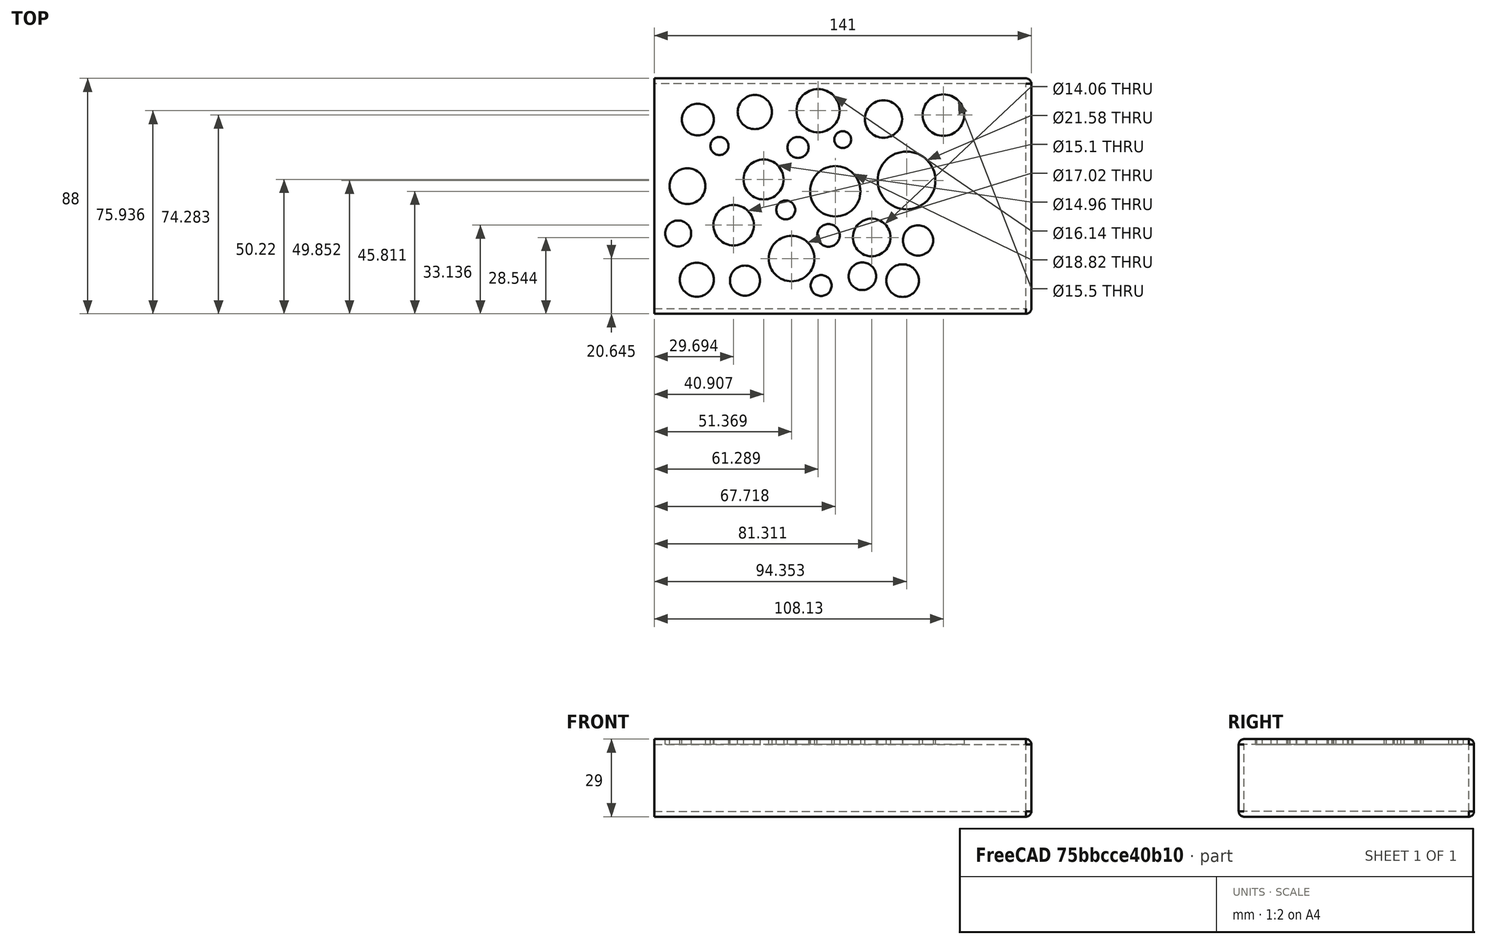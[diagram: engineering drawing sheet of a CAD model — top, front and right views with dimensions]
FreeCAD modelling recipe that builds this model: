
FCSTD DOCUMENT  (FreeCAD 0.18R4 (GitTag))
Label: V4
License: All rights reserved
LicenseURL: http://en.wikipedia.org/wiki/All_rights_reserved
objects: Sketcher::SketchObject×2, PartDesign::Pad×1, PartDesign::Thickness×1, PartDesign::Pocket×1, PartDesign::Body×1
note: 8 computed .brp shape members not serialized (recipe doc carries the construction recipe); baked Part::Feature solids carry a one-line shape summary decoded from their .brp

FEATURE [Sketcher::SketchObject] Sketch001
  MapMode = 5
  sketch-geometry (4):
    g0: LineSegment StartX=-98.6361 StartY=-55.4136 StartZ=0 EndX=40.3639 EndY=-55.4136 EndZ=0
    g1: LineSegment StartX=40.3639 StartY=-55.4136 StartZ=0 EndX=40.3639 EndY=28.5864 EndZ=0
    g2: LineSegment StartX=40.3639 StartY=28.5864 StartZ=0 EndX=-98.6361 EndY=28.5864 EndZ=0
    g3: LineSegment StartX=-98.6361 StartY=28.5864 StartZ=0 EndX=-98.6361 EndY=-55.4136 EndZ=0
  constraints (10):
    c: Coincident(g0,g1)
    c: Coincident(g1,g2)
    c: Coincident(g2,g3)
    c: Coincident(g3,g0)
    c: Horizontal(g0)
    c: Horizontal(g2)
    c: Vertical(g1)
    c: Vertical(g3)
    c: DistanceY(g0,g1) = 84
    c: DistanceX(g2,g1) = 139
FEATURE [PartDesign::Pad] Pad
  Length = 25
  Length2 = 100
  Profile = -> Sketch001
  Type = 0
FEATURE [PartDesign::Thickness] Thickness
  Base = -> Pad [Face4]
  BaseFeature = -> Pad
  Join = 0
  Mode = 0
  Value = 2
FEATURE [Sketcher::SketchObject] Sketch002
  MapMode = 5
  Placement = pos=(0,0,27) rot=(0,0,1;0rad)
  Support = -> [Thickness]
  sketch-geometry (24):
    g0: Circle CenterX=-82.3346 CenterY=15.2163 CenterZ=0 NormalX=0 NormalY=0 NormalZ=1 AngleXU=0 Radius=5.94705
    g1: Circle CenterX=-61.0213 CenterY=18.0212 CenterZ=0 NormalX=0 NormalY=0 NormalZ=1 AngleXU=0 Radius=6.39154
    g2: Circle CenterX=-57.7329 CenterY=-7.18999 CenterZ=0 NormalX=0 NormalY=0 NormalZ=1 AngleXU=0 Radius=7.47971
    g3: Circle CenterX=-86.2325 CenterY=-9.65631 CenterZ=0 NormalX=0 NormalY=0 NormalZ=1 AngleXU=0 Radius=6.69004
    g4: Circle CenterX=-68.9463 CenterY=-24.274 CenterZ=0 NormalX=0 NormalY=0 NormalZ=1 AngleXU=0 Radius=7.55147
    g5: Circle CenterX=-82.7231 CenterY=-44.6637 CenterZ=0 NormalX=0 NormalY=0 NormalZ=1 AngleXU=0 Radius=6.34199
    g6: Circle CenterX=-47.2707 CenterY=-36.765 CenterZ=0 NormalX=0 NormalY=0 NormalZ=1 AngleXU=0 Radius=8.50949
    g7: Circle CenterX=-30.9222 CenterY=-11.5993 CenterZ=0 NormalX=0 NormalY=0 NormalZ=1 AngleXU=0 Radius=9.40958
    g8: Circle CenterX=-37.3514 CenterY=18.526 CenterZ=0 NormalX=0 NormalY=0 NormalZ=1 AngleXU=0 Radius=8.06988
    g9: Circle CenterX=-17.3291 CenterY=-28.8663 CenterZ=0 NormalX=0 NormalY=0 NormalZ=1 AngleXU=0 Radius=7.03083
    g10: Circle CenterX=-20.8192 CenterY=-43.3779 CenterZ=0 NormalX=0 NormalY=0 NormalZ=1 AngleXU=0 Radius=5.14662
    g11: Circle CenterX=-12.9205 CenterY=15.4033 CenterZ=0 NormalX=0 NormalY=0 NormalZ=1 AngleXU=0 Radius=6.98267
    g12: Circle CenterX=9.48984 CenterY=16.8728 CenterZ=0 NormalX=0 NormalY=0 NormalZ=1 AngleXU=0 Radius=7.75212
    g13: Circle CenterX=-4.28699 CenterY=-7.55813 CenterZ=0 NormalX=0 NormalY=0 NormalZ=1 AngleXU=0 Radius=10.7878
    g14: Circle CenterX=0 CenterY=-29.9684 CenterZ=0 NormalX=0 NormalY=0 NormalZ=1 AngleXU=0 Radius=5.65876
    g15: Circle CenterX=-44.8587 CenterY=4.77725 CenterZ=0 NormalX=0 NormalY=0 NormalZ=1 AngleXU=0 Radius=3.93116
    g16: Circle CenterX=-74.2492 CenterY=5.32832 CenterZ=0 NormalX=0 NormalY=0 NormalZ=1 AngleXU=0 Radius=3.37712
    g17: Circle CenterX=-64.6973 CenterY=-45.003 CenterZ=0 NormalX=0 NormalY=0 NormalZ=1 AngleXU=0 Radius=5.62287
    g18: Circle CenterX=-36.2252 CenterY=-46.84 CenterZ=0 NormalX=0 NormalY=0 NormalZ=1 AngleXU=0 Radius=3.90532
    g19: Circle CenterX=-33.4698 CenterY=-28.1035 CenterZ=0 NormalX=0 NormalY=0 NormalZ=1 AngleXU=0 Radius=4.22889
    g20: Circle CenterX=-49.4509 CenterY=-18.5515 CenterZ=0 NormalX=0 NormalY=0 NormalZ=1 AngleXU=0 Radius=3.52859
    g21: Circle CenterX=-28.1428 CenterY=7.71631 CenterZ=0 NormalX=0 NormalY=0 NormalZ=1 AngleXU=0 Radius=3.16034
    g22: Circle CenterX=-5.73246 CenterY=-45.003 CenterZ=0 NormalX=0 NormalY=0 NormalZ=1 AngleXU=0 Radius=6.10618
    g23: Circle CenterX=-89.6793 CenterY=-27.3687 CenterZ=0 NormalX=0 NormalY=0 NormalZ=1 AngleXU=0 Radius=4.85306
  constraints (1):
    c: PointOnObject(g14,g-2)
FEATURE [PartDesign::Pocket] Pocket
  BaseFeature = -> Thickness
  Length = 5
  Length2 = 100
  Profile = -> Sketch002
  Type = 0
FEATURE [PartDesign::Body] Body001
  Group = -> [Sketch001,Pad,Thickness,Sketch002,Pocket]
  Origin = -> Origin001
  Tip = -> Pocket
